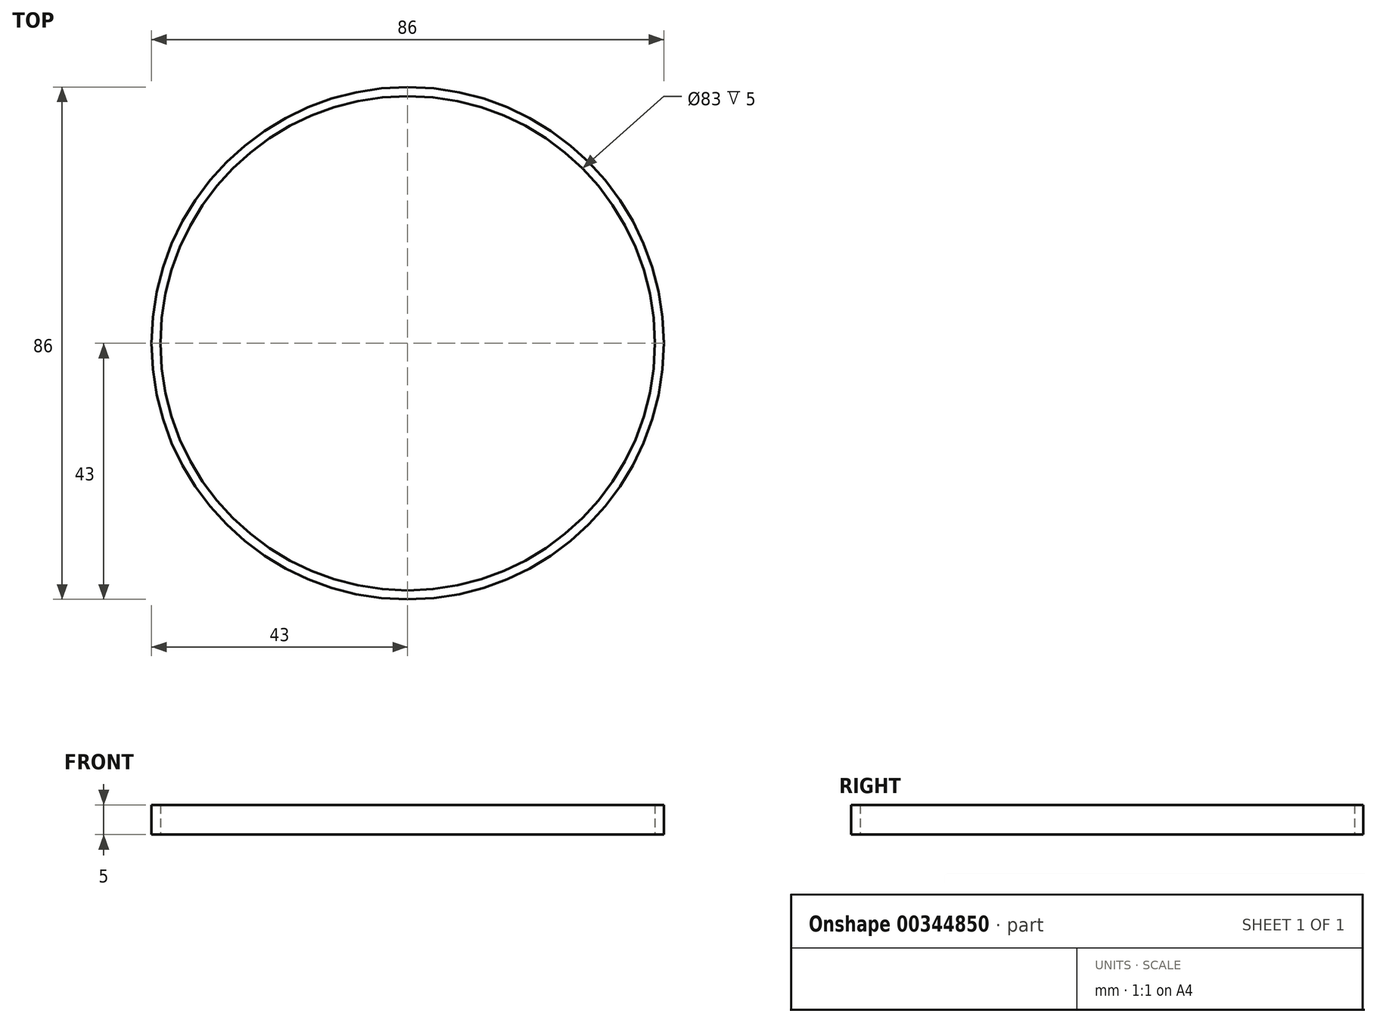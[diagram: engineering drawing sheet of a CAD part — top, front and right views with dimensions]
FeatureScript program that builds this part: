
annotation { "Feature Type Name" : "Feature", "Feature Type Description" : "" }
export const myFeature = defineFeature(function(context is Context, id is Id, definition is map)
    precondition{}
    {
        {
            var Q0;
            Q0=qCreatedBy(makeId("Top.planeOp"),FACE);
            var sketch = newSketch(context, id + "F0", { "sketchPlane" : qUnion([Q0])});
            skCircle(sketch, "E0", {"center": v(0, 0) * mm, "radius": 41.5 * mm});
            skCircle(sketch, "E1", {"center": v(0, 0) * mm, "radius": 43 * mm});
            skSolve(sketch);
        }
        {
            var Q0;
            Q0=makeQuery(id+"F0.imprint","IMPRINT",FACE,{"disambiguationData":[TD([[makeQuery(id+"F0.imprint","IMPRINT",EDGE,{"derivedFrom":sQuery(id+"F0.wireOp",EDGE,"E0")}),-1.0]])]});
            extrude(context, id + "F1", {"entities" : qUnion([Q0]), "depth" : 5 * mm});
        }
    });
